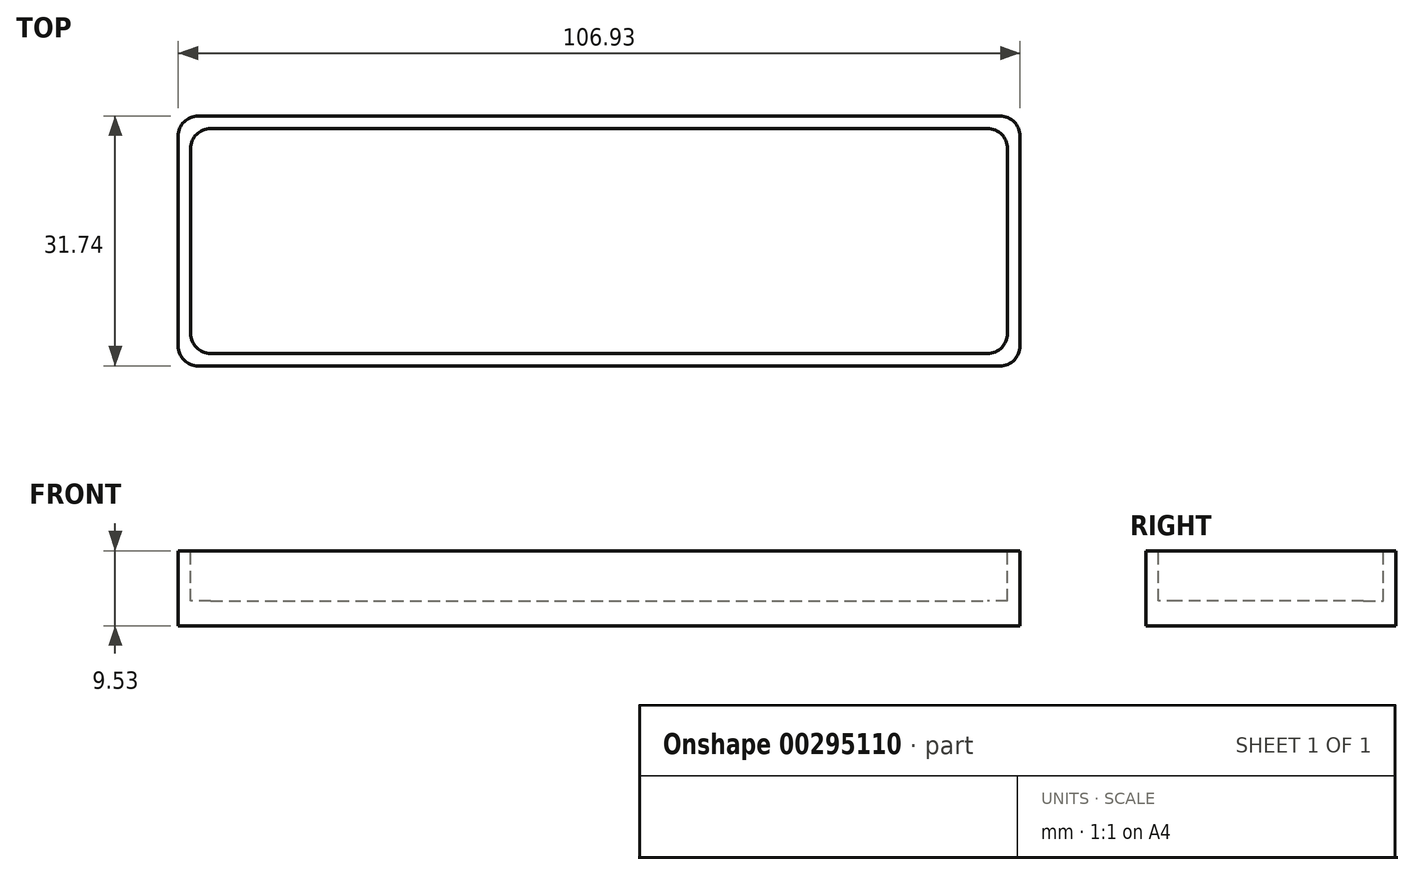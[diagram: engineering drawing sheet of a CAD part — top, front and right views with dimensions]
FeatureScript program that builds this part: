
annotation { "Feature Type Name" : "Feature", "Feature Type Description" : "" }
export const myFeature = defineFeature(function(context is Context, id is Id, definition is map)
    precondition{}
    {
        {
            var Q0;
            Q0=qCreatedBy(makeId("Top.planeOp"),FACE);
            var sketch = newSketch(context, id + "F0", { "sketchPlane" : qUnion([Q0])});
            skLineSegment(sketch, "E0.bottom", {"start": v(0, 0) * mm, "end": v(100.58, 0) * mm});
            skLineSegment(sketch, "E0.top", {"start": v(0, 25.4) * mm, "end": v(100.58, 25.4) * mm});
            skLineSegment(sketch, "E0.left", {"start": v(0, 0) * mm, "end": v(0, 25.4) * mm});
            skLineSegment(sketch, "E0.right", {"start": v(100.58, 0) * mm, "end": v(100.58, 25.4) * mm});
            skLineSegment(sketch, "E1.bottom", {"start": v(-3.17, -3.18) * mm, "end": v(103.76, -3.18) * mm});
            skLineSegment(sketch, "E1.top", {"start": v(-3.18, 28.58) * mm, "end": v(103.76, 28.58) * mm});
            skLineSegment(sketch, "E1.left", {"start": v(-3.17, -3.18) * mm, "end": v(-3.18, 28.58) * mm});
            skLineSegment(sketch, "E1.right", {"start": v(103.76, -3.18) * mm, "end": v(103.76, 28.58) * mm});
            skSolve(sketch);
        }
        {
            var Q0;
            Q0=makeQuery(id+"F0.imprint","IMPRINT",FACE,{"disambiguationData":[TD([[makeQuery(id+"F0.imprint","IMPRINT",EDGE,{"derivedFrom":sQuery(id+"F0.wireOp",EDGE,"E0.bottom")}),1.0]])]});
            extrude(context, id + "F1", {"entities" : qUnion([Q0]), "depth" : 3.17 * mm});
        }
        {
            var Q0;
            Q0=makeQuery(id+"F0.imprint","IMPRINT",FACE,{"disambiguationData":[TD([[makeQuery(id+"F0.imprint","IMPRINT",EDGE,{"derivedFrom":sQuery(id+"F0.wireOp",EDGE,"E0.bottom")}),-1.0]])]});
            extrude(context, id + "F2", {"entities" : qUnion([Q0]), "operationType" : NewBodyOperationType.ADD, "depth" : 9.52 * mm});
        }
        {
            var Q0;
            Q0=makeQuery(id+"F2.opExtrude","CAP_FACE",FACE,{"disambiguationData":[OSD([sQuery(id+"F0.wireOp",EDGE,"E0.bottom"),sQuery(id+"F0.wireOp",EDGE,"E0.top"),sQuery(id+"F0.wireOp",EDGE,"E0.left"),sQuery(id+"F0.wireOp",EDGE,"E0.right"),sQuery(id+"F0.wireOp",EDGE,"E1.bottom"),sQuery(id+"F0.wireOp",EDGE,"E1.top"),sQuery(id+"F0.wireOp",EDGE,"E1.left"),sQuery(id+"F0.wireOp",EDGE,"E1.right")])],"isStart":false});
            var sketch = newSketch(context, id + "F3", { "sketchPlane" : qUnion([Q0])});
            skLineSegment(sketch, "E2.bottom", {"start": v(-1.59, 26.99) * mm, "end": v(102.17, 26.99) * mm});
            skLineSegment(sketch, "E2.top", {"start": v(-1.59, -1.59) * mm, "end": v(102.17, -1.59) * mm});
            skLineSegment(sketch, "E2.left", {"start": v(-1.59, 26.99) * mm, "end": v(-1.59, -1.59) * mm});
            skLineSegment(sketch, "E2.right", {"start": v(102.17, 26.99) * mm, "end": v(102.17, -1.59) * mm});
            skSolve(sketch);
        }
        {
            var Q0;
            Q0=makeQuery(id+"F3.imprint","IMPRINT",FACE,{"disambiguationData":[TD([[makeQuery(id+"F3.imprint","IMPRINT",EDGE,{"derivedFrom":sQuery(id+"F3.wireOp",EDGE,"E2.bottom")}),-1.0]])]});
            extrude(context, id + "F4", {"entities" : qUnion([Q0]), "operationType" : NewBodyOperationType.REMOVE, "oppositeDirection" : true, "depth" : 6.35 * mm});
        }
        {
            var Q0;
            Q0=makeQuery(id+"F4.boolean.opBoolean","COPY",EDGE,{"derivedFrom":makeQuery(id+"F4.opExtrude","SWEPT_EDGE",EDGE,{"disambiguationData":[OSD([sQuery(id+"F3.wireOp",EDGE,"E2.bottom"),sQuery(id+"F3.wireOp",EDGE,"E2.left")])]})});
            var Q1;
            Q1=makeQuery(id+"F4.boolean.opBoolean","COPY",EDGE,{"derivedFrom":makeQuery(id+"F4.opExtrude","SWEPT_EDGE",EDGE,{"disambiguationData":[OSD([sQuery(id+"F3.wireOp",EDGE,"E2.top"),sQuery(id+"F3.wireOp",EDGE,"E2.left")])]})});
            var Q2;
            Q2=makeQuery(id+"F4.boolean.opBoolean","COPY",EDGE,{"derivedFrom":makeQuery(id+"F4.opExtrude","SWEPT_EDGE",EDGE,{"disambiguationData":[OSD([sQuery(id+"F3.wireOp",EDGE,"E2.top"),sQuery(id+"F3.wireOp",EDGE,"E2.right")])]})});
            var Q3;
            Q3=makeQuery(id+"F4.boolean.opBoolean","COPY",EDGE,{"derivedFrom":makeQuery(id+"F4.opExtrude","SWEPT_EDGE",EDGE,{"disambiguationData":[OSD([sQuery(id+"F3.wireOp",EDGE,"E2.bottom"),sQuery(id+"F3.wireOp",EDGE,"E2.right")])]})});
            var Q4;
            Q4=makeQuery(id+"F2.opExtrude","SWEPT_EDGE",EDGE,{"disambiguationData":[OSD([sQuery(id+"F0.wireOp",EDGE,"E1.bottom"),sQuery(id+"F0.wireOp",EDGE,"E1.left")])]});
            var Q5;
            Q5=makeQuery(id+"F2.opExtrude","SWEPT_EDGE",EDGE,{"disambiguationData":[OSD([sQuery(id+"F0.wireOp",EDGE,"E1.bottom"),sQuery(id+"F0.wireOp",EDGE,"E1.right")])]});
            var Q6;
            Q6=makeQuery(id+"F2.opExtrude","SWEPT_EDGE",EDGE,{"disambiguationData":[OSD([sQuery(id+"F0.wireOp",EDGE,"E1.top"),sQuery(id+"F0.wireOp",EDGE,"E1.right")])]});
            var Q7;
            Q7=makeQuery(id+"F2.opExtrude","SWEPT_EDGE",EDGE,{"disambiguationData":[OSD([sQuery(id+"F0.wireOp",EDGE,"E1.top"),sQuery(id+"F0.wireOp",EDGE,"E1.left")])]});
            fillet(context, id + "F5", {"entities" : qUnion([Q0, Q1, Q2, Q3, Q4, Q5, Q6, Q7]), "radius" : 2.54 * mm, "tangentPropagation" : true, "allowEdgeOverflow" : false});
        }
    });
